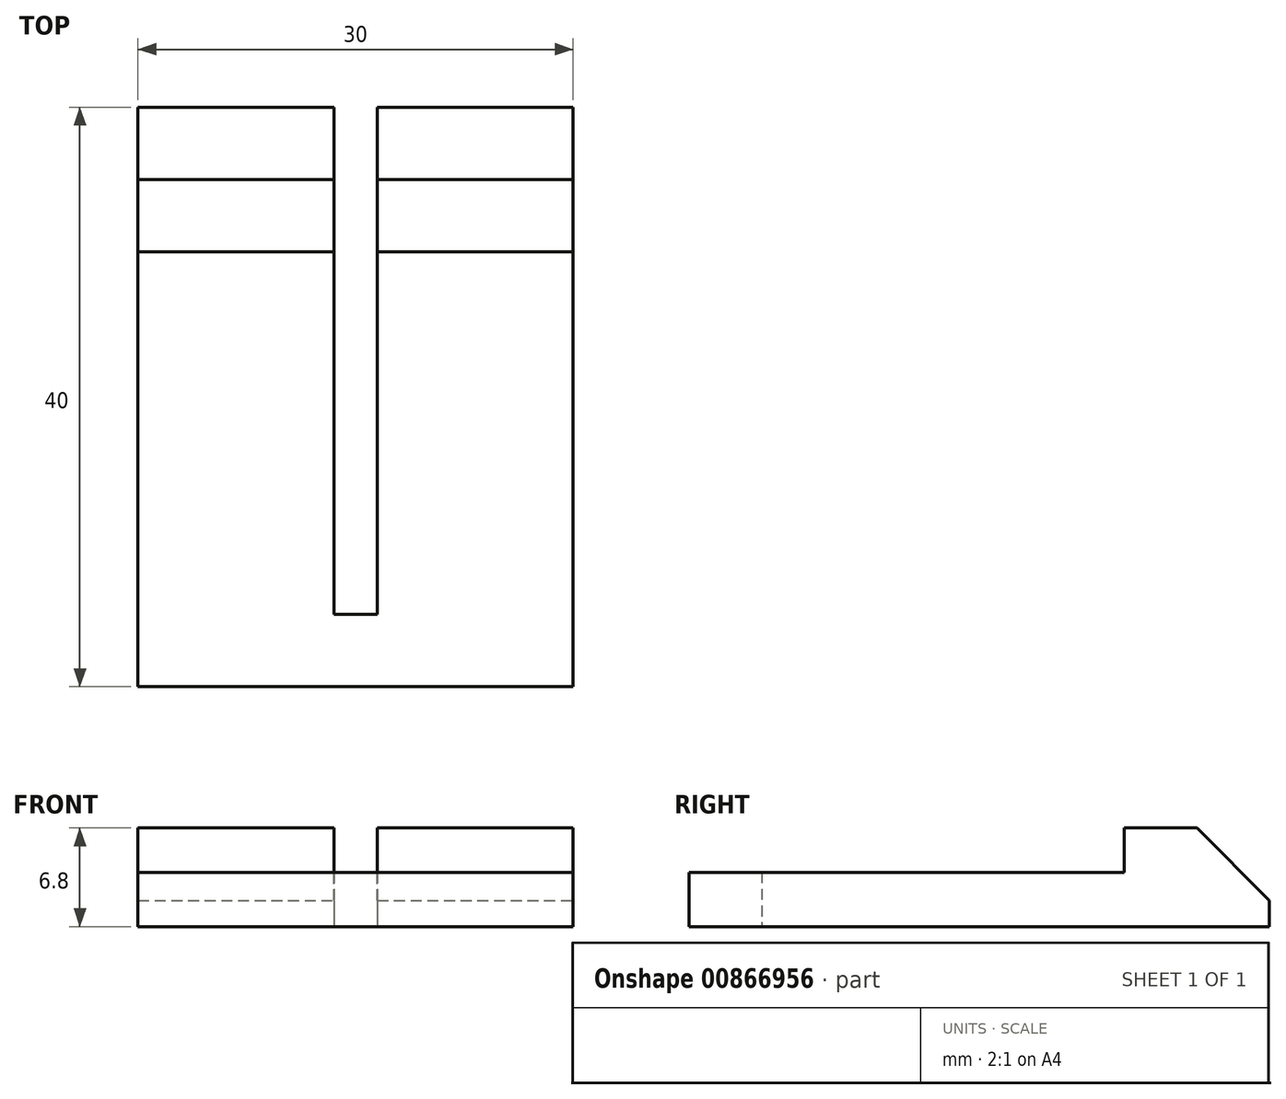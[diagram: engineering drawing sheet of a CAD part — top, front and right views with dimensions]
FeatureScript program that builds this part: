
annotation { "Feature Type Name" : "Feature", "Feature Type Description" : "" }
export const myFeature = defineFeature(function(context is Context, id is Id, definition is map)
    precondition{}
    {
        {
            var Q0;
            Q0=qCreatedBy(makeId("Top.planeOp"),FACE);
            var sketch = newSketch(context, id + "F0", { "sketchPlane" : qUnion([Q0])});
            skLineSegment(sketch, "E0", {"start": v(0, 0) * mm, "end": v(15, 0) * mm});
            skLineSegment(sketch, "E1", {"start": v(0, 0) * mm, "end": v(-15, 0) * mm});
            skLineSegment(sketch, "E2", {"start": v(0, 5) * mm, "end": v(0, 0) * mm});
            skLineSegment(sketch, "E3", {"start": v(1.5, 5) * mm, "end": v(-1.5, 5) * mm});
            skLineSegment(sketch, "E4", {"start": v(-1.5, 5) * mm, "end": v(-1.5, 0) * mm});
            skLineSegment(sketch, "E5", {"start": v(1.5, 5) * mm, "end": v(1.5, 0) * mm});
            skLineSegment(sketch, "E6", {"start": v(-1.5, 5) * mm, "end": v(-15, 5) * mm});
            skLineSegment(sketch, "E7", {"start": v(1.5, 5) * mm, "end": v(15, 4.92) * mm});
            skLineSegment(sketch, "E8", {"start": v(-15, 0) * mm, "end": v(-15, 40) * mm});
            skLineSegment(sketch, "E9", {"start": v(15, 0) * mm, "end": v(15, 40) * mm});
            skLineSegment(sketch, "E10", {"start": v(-1.5, 5) * mm, "end": v(-1.5, 40) * mm});
            skLineSegment(sketch, "E11", {"start": v(-1.5, 40) * mm, "end": v(-15, 40) * mm});
            skLineSegment(sketch, "E12", {"start": v(1.5, 5) * mm, "end": v(1.5, 40) * mm});
            skLineSegment(sketch, "E13", {"start": v(1.5, 40) * mm, "end": v(15, 40) * mm});
            skLineSegment(sketch, "E14", {"start": v(-15, 30) * mm, "end": v(-1.5, 30) * mm});
            skLineSegment(sketch, "E15", {"start": v(1.5, 30) * mm, "end": v(15, 30) * mm});
            skSolve(sketch);
        }
        {
            var Q0;
            {var subQ0=sQuery(id+"F0.wireOp",EDGE,"E6");Q0=makeQuery(id+"F0.imprint","IMPRINT",FACE,{"disambiguationData":[TD([[makeQuery(id+"F0.imprint","IMPRINT",EDGE,{"derivedFrom":subQ0}),-1.0]])]});}
            var Q1;
            {var subQ0=sQuery(id+"F0.wireOp",EDGE,"E7");Q1=makeQuery(id+"F0.imprint","IMPRINT",FACE,{"disambiguationData":[TD([[makeQuery(id+"F0.imprint","IMPRINT",EDGE,{"derivedFrom":subQ0}),1.0]])]});}
            var Q2;
            {var subQ3=sQuery(id+"F0.wireOp",EDGE,"E5");Q2=makeQuery(id+"F0.imprint","IMPRINT",FACE,{"disambiguationData":[TD([[makeQuery(id+"F0.imprint","IMPRINT",EDGE,{"derivedFrom":subQ3}),1.0]])]});}
            var Q3;
            {var subQ0=sQuery(id+"F0.wireOp",EDGE,"E2");Q3=makeQuery(id+"F0.imprint","IMPRINT",FACE,{"disambiguationData":[TD([[makeQuery(id+"F0.imprint","IMPRINT",EDGE,{"derivedFrom":subQ0}),1.0]])]});}
            var Q4;
            {var subQ0=sQuery(id+"F0.wireOp",EDGE,"E2");Q4=makeQuery(id+"F0.imprint","IMPRINT",FACE,{"disambiguationData":[TD([[makeQuery(id+"F0.imprint","IMPRINT",EDGE,{"derivedFrom":subQ0}),-1.0]])]});}
            var Q5;
            {var subQ3=sQuery(id+"F0.wireOp",EDGE,"E4");Q5=makeQuery(id+"F0.imprint","IMPRINT",FACE,{"disambiguationData":[TD([[makeQuery(id+"F0.imprint","IMPRINT",EDGE,{"derivedFrom":subQ3}),-1.0]])]});}
            extrude(context, id + "F1", {"entities" : qUnion([Q0, Q1, Q2, Q3, Q4, Q5]), "depth" : 3.75 * mm, "offsetDistance" : 25 * mm});
        }
        {
            var Q0;
            {var subQ0=sQuery(id+"F0.wireOp",EDGE,"E11");Q0=makeQuery(id+"F0.imprint","IMPRINT",FACE,{"disambiguationData":[TD([[makeQuery(id+"F0.imprint","IMPRINT",EDGE,{"derivedFrom":subQ0}),1.0]])]});}
            var Q1;
            {var subQ0=sQuery(id+"F0.wireOp",EDGE,"E13");Q1=makeQuery(id+"F0.imprint","IMPRINT",FACE,{"disambiguationData":[TD([[makeQuery(id+"F0.imprint","IMPRINT",EDGE,{"derivedFrom":subQ0}),-1.0]])]});}
            extrude(context, id + "F2", {"entities" : qUnion([Q0, Q1]), "operationType" : NewBodyOperationType.ADD, "depth" : 6.8 * mm, "offsetDistance" : 25 * mm});
        }
        {
            var Q0;
            Q0=makeQuery(id+"F2.opExtrude","CAP_EDGE",EDGE,{"disambiguationData":[OSD([sQuery(id+"F0.wireOp",EDGE,"E11")])],"isStart":false});
            var Q1;
            Q1=makeQuery(id+"F2.opExtrude","CAP_EDGE",EDGE,{"disambiguationData":[OSD([sQuery(id+"F0.wireOp",EDGE,"E13")])],"isStart":false});
            var Q2;
            Q2=makeQuery(id+"FHTjjfoAzYWYuMv_4.opExtrude","CAP_EDGE",EDGE,{"disambiguationData":[OSD([sQuery(id+"F0.wireOp",EDGE,"E13")])],"isStart":false});
            var Q3;
            Q3=makeQuery(id+"FHTjjfoAzYWYuMv_4.opExtrude","CAP_EDGE",EDGE,{"disambiguationData":[OSD([sQuery(id+"F0.wireOp",EDGE,"E11")])],"isStart":false});
            chamfer(context, id + "F3", {"entities" : qUnion([Q0, Q1, Q2, Q3]), "width" : 5 * mm, "tangentPropagation" : true});
        }
    });
